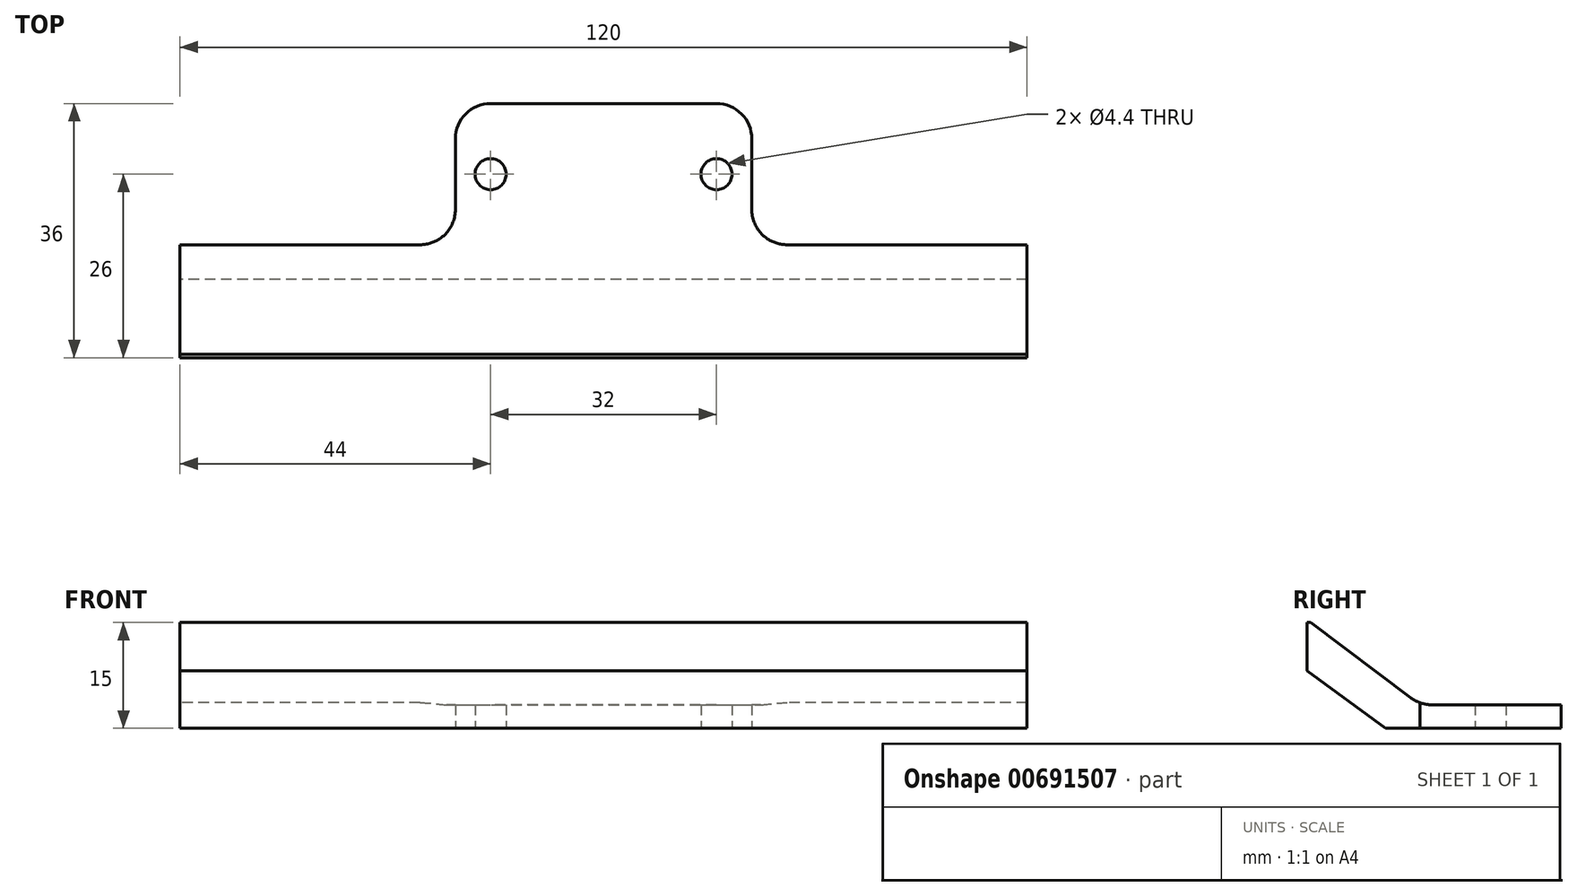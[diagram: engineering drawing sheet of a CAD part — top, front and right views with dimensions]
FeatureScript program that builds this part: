
annotation { "Feature Type Name" : "Feature", "Feature Type Description" : "" }
export const myFeature = defineFeature(function(context is Context, id is Id, definition is map)
    precondition{}
    {
        {
            var Q0;
            Q0=qCreatedBy(makeId("Top.planeOp"),FACE);
            var sketch = newSketch(context, id + "F0", { "sketchPlane" : qUnion([Q0])});
            skLineSegment(sketch, "E0", {"start": v(0, 20) * mm, "end": v(-21, 20) * mm});
            skLineSegment(sketch, "E1", {"start": v(-21, 20) * mm, "end": v(-21, 0) * mm});
            skLineSegment(sketch, "E2", {"start": v(-21, 0) * mm, "end": v(-60, 0) * mm});
            skLineSegment(sketch, "E3", {"start": v(-60, 0) * mm, "end": v(-60, -16) * mm});
            skLineSegment(sketch, "E4", {"start": v(-60, -16) * mm, "end": v(0, -16) * mm});
            skLineSegment(sketch, "E5.MirrorCS", {"start": v(60, -16) * mm, "end": v(0, -16) * mm});
            skLineSegment(sketch, "E6.MirrorCS", {"start": v(60, 0) * mm, "end": v(60, -16) * mm});
            skLineSegment(sketch, "E7.MirrorCS", {"start": v(21, 0) * mm, "end": v(60, 0) * mm});
            skLineSegment(sketch, "E8.MirrorCS", {"start": v(0, 20) * mm, "end": v(21, 20) * mm});
            skLineSegment(sketch, "E9.MirrorCS", {"start": v(21, 20) * mm, "end": v(21, 0) * mm});
            skPoint(sketch, "E10", {"position": v(-16, 10) * mm});
            skPoint(sketch, "E10.positionSnap0", {"position": v(-21, 10) * mm});
            skPoint(sketch, "E11.MirrorP", {"position": v(16, 10) * mm});
            skSolve(sketch);
        }
        {
            var Q0;
            Q0=makeQuery(id+"F0.imprint","IMPRINT",FACE,{"disambiguationData":[TD([[makeQuery(id+"F0.imprint","IMPRINT",EDGE,{"derivedFrom":sQuery(id+"F0.wireOp",EDGE,"E0")}),1.0]])]});
            extrude(context, id + "F1", {"entities" : qUnion([Q0]), "depth" : 15 * mm, "offsetDistance" : 25 * mm});
        }
        {
            var Q0;
            Q0=qCreatedBy(makeId("Right.planeOp"),FACE);
            var sketch = newSketch(context, id + "F2", { "sketchPlane" : qUnion([Q0])});
            skLineSegment(sketch, "E12", {"start": v(-15.96, 15.32) * mm, "end": v(0, 3.34) * mm});
            skLineSegment(sketch, "E13", {"start": v(0, 3.34) * mm, "end": v(26.68, 3.34) * mm});
            skLineSegment(sketch, "E14", {"start": v(26.68, 15.84) * mm, "end": v(26.68, 3.34) * mm});
            skLineSegment(sketch, "E15", {"start": v(26.68, 15.84) * mm, "end": v(-2.37, 15.84) * mm});
            skLineSegment(sketch, "E16", {"start": v(-2.37, 15.84) * mm, "end": v(-12.24, 23.25) * mm});
            skLineSegment(sketch, "E17", {"start": v(-15.96, 15.32) * mm, "end": v(-12.24, 23.25) * mm});
            skLineSegment(sketch, "E18", {"start": v(0, -3.58) * mm, "end": v(-18.65, 10.09) * mm});
            skLineSegment(sketch, "E19", {"start": v(-18.65, 10.09) * mm, "end": v(-18.65, -3.58) * mm});
            skLineSegment(sketch, "E20", {"start": v(-18.65, -3.58) * mm, "end": v(1.05, -3.58) * mm});
            skSolve(sketch);
        }
        {
            var Q0;
            Q0=makeQuery(id+"F2.imprint","IMPRINT",FACE,{"disambiguationData":[TD([[makeQuery(id+"F2.imprint","IMPRINT",EDGE,{"derivedFrom":sQuery(id+"F2.wireOp",EDGE,"E12")}),1.0]])]});
            var Q1;
            {var subQ0=sQuery(id+"F2.wireOp",EDGE,"E18");Q1=makeQuery(id+"F2.imprint","IMPRINT",FACE,{"disambiguationData":[TD([[makeQuery(id+"F2.imprint","IMPRINT",EDGE,{"derivedFrom":subQ0}),1.0]])]});}
            extrude(context, id + "F3", {"entities" : qUnion([Q0, Q1]), "operationType" : NewBodyOperationType.REMOVE, "oppositeDirection" : true, "depth" : 100 * mm, "offsetDistance" : 25 * mm, "hasSecondDirection" : true, "secondDirectionOppositeDirection" : false, "secondDirectionDepth" : 100 * mm});
        }
        {
            var Q0;
            Q0=sQuery(id+"F0.wireOp",VERTEX,"E10");
            var Q1;
            Q1=sQuery(id+"F0.wireOp",VERTEX,"E11.MirrorP");
            var Q2;
            Q2=makeQuery(id+"F1.opExtrude","SWEPT_BODY",BODY,{"disambiguationData":[OSD([sQuery(id+"F0.wireOp",EDGE,"E0"),sQuery(id+"F0.wireOp",EDGE,"E1"),sQuery(id+"F0.wireOp",EDGE,"E2"),sQuery(id+"F0.wireOp",EDGE,"E3"),sQuery(id+"F0.wireOp",EDGE,"E4"),sQuery(id+"F0.wireOp",EDGE,"E5.MirrorCS"),sQuery(id+"F0.wireOp",EDGE,"E6.MirrorCS"),sQuery(id+"F0.wireOp",EDGE,"E7.MirrorCS"),sQuery(id+"F0.wireOp",EDGE,"E8.MirrorCS"),sQuery(id+"F0.wireOp",EDGE,"E9.MirrorCS")])]});
            hole(context, id + "F4", {"style" : HoleStyle.SIMPLE, "endStyle" : HoleEndStyle.THROUGH, "oppositeDirection" : true, "standardTappedOrClearance" : lookupTablePath({ "standard" : "ISO", "fit" : "Normal", "size" : "M4", "type" : "Clearance" }), "standardBlindInLast" : lookupTablePath({ "fit" : "Standard", "standard" : "ISO", "size" : "M4", "type" : "Clearance" }), "holeDiameter" : 4.4 * mm, "majorDiameter" : 3 * mm, "isTappedThrough" : true, "tappedDepth" : 12 * mm, "tapClearance" : 3, "startFromSketch" : true, "locations" : qUnion([Q0, Q1]), "scope" : qUnion([Q2])});
        }
        {
            var Q0;
            Q0=makeQuery(id+"F1.opExtrude","SWEPT_EDGE",EDGE,{"disambiguationData":[OSD([sQuery(id+"F0.wireOp",EDGE,"E1"),sQuery(id+"F0.wireOp",EDGE,"E2")])]});
            var Q1;
            Q1=makeQuery(id+"F1.opExtrude","SWEPT_EDGE",EDGE,{"disambiguationData":[OSD([sQuery(id+"F0.wireOp",EDGE,"E7.MirrorCS"),sQuery(id+"F0.wireOp",EDGE,"E9.MirrorCS")])]});
            var Q2;
            Q2=makeQuery(id+"F1.opExtrude","SWEPT_EDGE",EDGE,{"disambiguationData":[OSD([sQuery(id+"F0.wireOp",EDGE,"E8.MirrorCS"),sQuery(id+"F0.wireOp",EDGE,"E9.MirrorCS")])]});
            var Q3;
            Q3=makeQuery(id+"F1.opExtrude","SWEPT_EDGE",EDGE,{"disambiguationData":[OSD([sQuery(id+"F0.wireOp",EDGE,"E0"),sQuery(id+"F0.wireOp",EDGE,"E1")])]});
            var Q4;
            {var subQ0=sQuery(id+"F2.wireOp",EDGE,"E12");var subQ1=sQuery(id+"F2.wireOp",EDGE,"E13");Q4=makeQuery(id+"F3.boolean.opBoolean","COPY",EDGE,{"disambiguationData":[topologyDisambiguationEdgeConnected([makeQuery(id+"F3.opExtrude","SWEPT_FACE",FACE,{"disambiguationData":[OSD([subQ1])]})])],"derivedFrom":makeQuery(id+"F3.opExtrude","SWEPT_EDGE",EDGE,{"disambiguationData":[OSD([subQ0,subQ1])]})});}
            fillet(context, id + "F5", {"entities" : qUnion([Q0, Q1, Q2, Q3, Q4]), "radius" : 5 * mm, "tangentPropagation" : true, "allowEdgeOverflow" : false});
        }
    });
